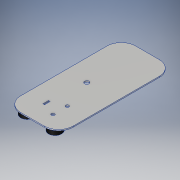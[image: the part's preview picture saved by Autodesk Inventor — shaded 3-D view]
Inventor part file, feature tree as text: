
AUTODESK INVENTOR PART (.ipt)
format: ipt  version: 2018 (Build 220112000, 112)  size: 166,400 bytes
history: native  units: in
note: dims shown in document units (in); Inventor stores cm internally (conversion verified against a paired STEP export)
features: extrude x2, sketch x2
ambient origin geometry x8: Origin, YZ Plane, XZ Plane, XY Plane, X Axis, Y Axis, Z Axis, Center Point
bodies: Solid1 (feature_tree)
feature tree (4):
  extrude  "Extrusion1"  Depth=0.5in
  extrude  "Extrusion2"  Depth=0.5in
  sketch  "Sketch1"  dims[d1=3.999in d2=0.5in]
  sketch  "Sketch2"  dims[d3=0.5in d4=0.5in d5=0.5in d6=0.5in d7=0.5in d8=0.5in d9=0.5in d10=1.82in d11=0.75in d12=1.95in d13=0.158in d14=0.058in d15=0.65in d16=0.192in d17=0.625in d18=0.5in d19=0.7in d20=0.5in d21=0.111in d22=0.111in d23=0.0385in d24=0.0in d25=0.425in d26=0.3in d27=0.45in d28=0.425in d29=0.45in d30=0.3in d31=0.45in d32=0.45in d33=0.05in d34=0.084in d35=0.2in d36=0.0in]
